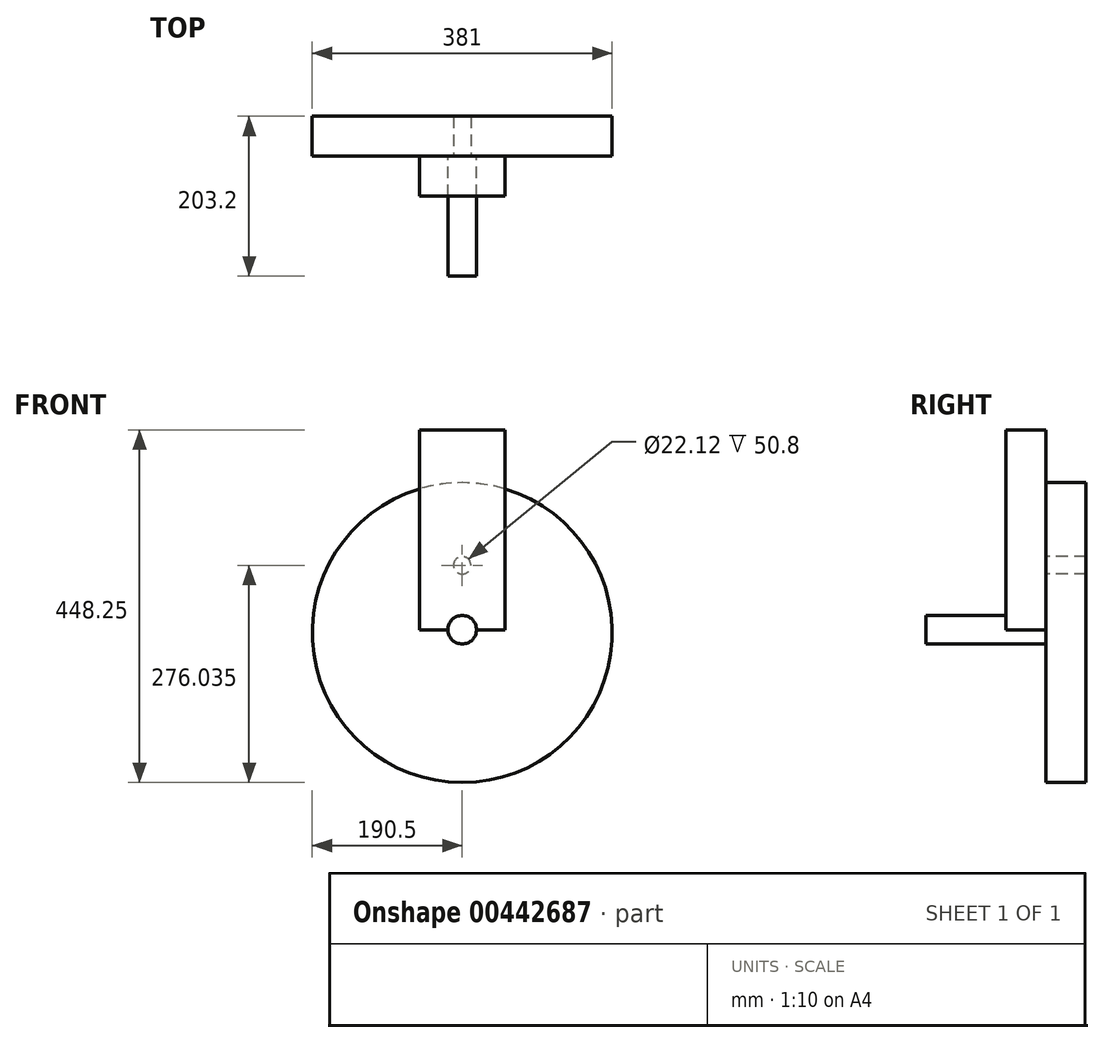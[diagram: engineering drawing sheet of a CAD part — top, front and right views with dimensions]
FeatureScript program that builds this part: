
annotation { "Feature Type Name" : "Feature", "Feature Type Description" : "" }
export const myFeature = defineFeature(function(context is Context, id is Id, definition is map)
    precondition{}
    {
        {
            var Q0;
            Q0=qCreatedBy(makeId("Front.planeOp"),FACE);
            var sketch = newSketch(context, id + "F0", { "sketchPlane" : qUnion([Q0])});
            skCircle(sketch, "E0", {"center": v(0, -132.51) * mm, "radius": 190.5 * mm});
            skSolve(sketch);
        }
        {
            var Q0;
            Q0 = qSketchRegion(id + "F0", true);
            extrude(context, id + "F1", {"entities" : qUnion([Q0]), "depth" : 50.8 * mm});
        }
        {
            var Q0;
            Q0=makeQuery(id+"F1.opExtrude","CAP_FACE",FACE,{"disambiguationData":[OSD([sQuery(id+"F0.wireOp",EDGE,"E0")])],"isStart":false});
            var sketch = newSketch(context, id + "F2", { "sketchPlane" : qUnion([Q0])});
            skCircle(sketch, "E1", {"center": v(0, -46.98) * mm, "radius": 11.06 * mm});
            skSolve(sketch);
        }
        {
            var Q0;
            Q0 = qSketchRegion(id + "F2", true);
            extrude(context, id + "F3", {"entities" : qUnion([Q0]), "operationType" : NewBodyOperationType.REMOVE, "oppositeDirection" : true, "depth" : 50.8 * mm});
        }
        {
            var Q0;
            Q0=makeQuery(id+"F1.opExtrude","CAP_FACE",FACE,{"disambiguationData":[OSD([sQuery(id+"F0.wireOp",EDGE,"E0")])],"isStart":false});
            var sketch = newSketch(context, id + "F4", { "sketchPlane" : qUnion([Q0])});
            skLineSegment(sketch, "E2.bottom", {"start": v(-54.55, -128.76) * mm, "end": v(54.55, -128.76) * mm});
            skLineSegment(sketch, "E2.top", {"start": v(-54.55, 125.24) * mm, "end": v(54.55, 125.24) * mm});
            skLineSegment(sketch, "E2.left", {"start": v(-54.55, -128.76) * mm, "end": v(-54.55, 125.24) * mm});
            skLineSegment(sketch, "E2.right", {"start": v(54.55, -128.76) * mm, "end": v(54.55, 125.24) * mm});
            skSolve(sketch);
        }
        {
            var Q0;
            Q0 = qSketchRegion(id + "F4", true);
            extrude(context, id + "F5", {"entities" : qUnion([Q0]), "operationType" : NewBodyOperationType.ADD, "depth" : 50.8 * mm});
        }
        {
            var Q0;
            Q0=makeQuery(id+"F1.opExtrude","CAP_FACE",FACE,{"disambiguationData":[OSD([sQuery(id+"F0.wireOp",EDGE,"E0")])],"isStart":false});
            var sketch = newSketch(context, id + "F6", { "sketchPlane" : qUnion([Q0])});
            skCircle(sketch, "E3", {"center": v(0, -128.76) * mm, "radius": 18.12 * mm});
            skSolve(sketch);
        }
        {
            var Q0;
            Q0 = qSketchRegion(id + "F6", true);
            extrude(context, id + "F7", {"entities" : qUnion([Q0]), "operationType" : NewBodyOperationType.ADD, "depth" : 152.4 * mm});
        }
    });
